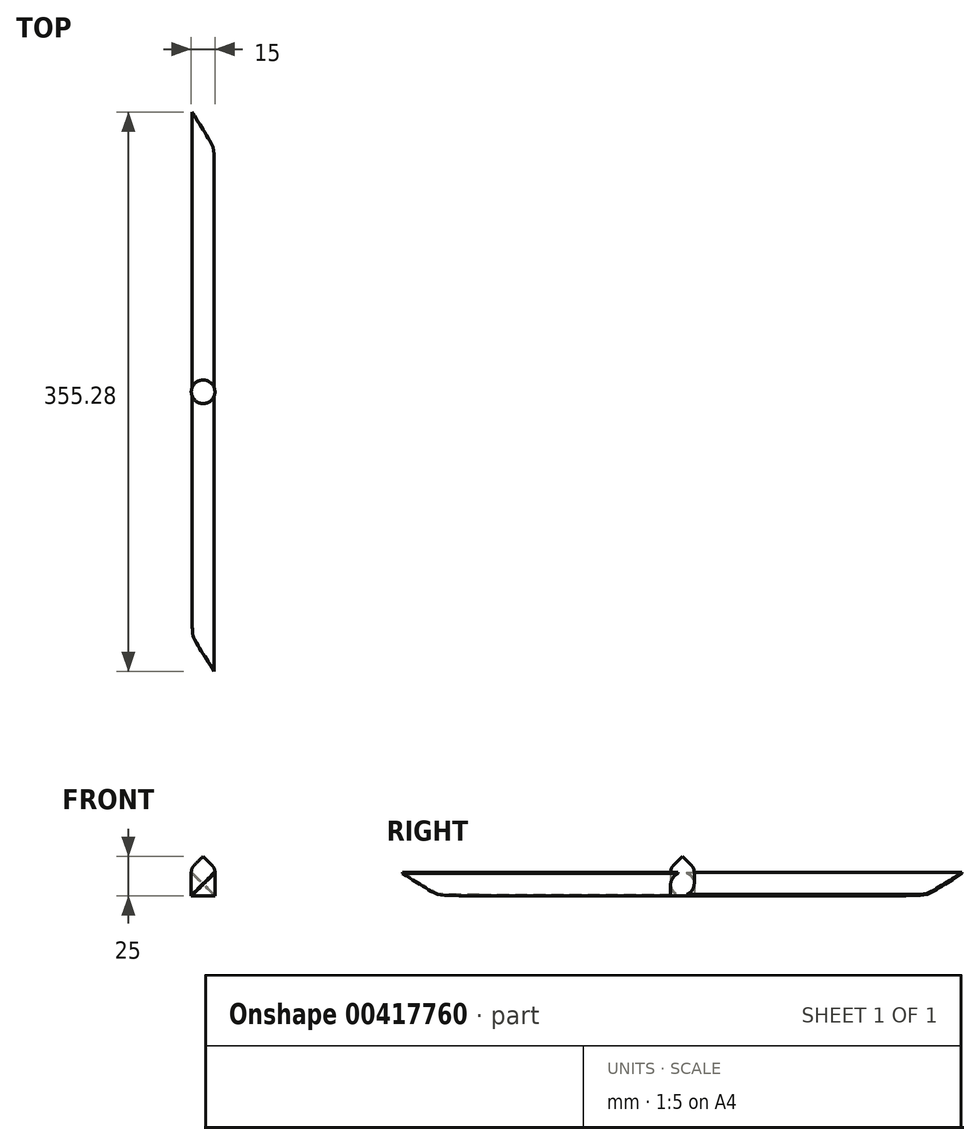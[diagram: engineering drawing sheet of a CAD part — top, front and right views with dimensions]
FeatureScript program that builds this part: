
annotation { "Feature Type Name" : "Feature", "Feature Type Description" : "" }
export const myFeature = defineFeature(function(context is Context, id is Id, definition is map)
    precondition{}
    {
        {
            var Q0;
            Q0=qCreatedBy(makeId("Top.planeOp"),FACE);
            var sketch = newSketch(context, id + "F0", { "sketchPlane" : qUnion([Q0])});
            skCircle(sketch, "E0", {"center": v(0, 0) * mm, "radius": 7.5 * mm});
            skLineSegment(sketch, "E1.bottom", {"start": v(7, -177.64) * mm, "end": v(-7, -177.64) * mm});
            skLineSegment(sketch, "E1.top", {"start": v(7, 177.64) * mm, "end": v(-7, 177.64) * mm});
            skLineSegment(sketch, "E1.left", {"start": v(7, -177.64) * mm, "end": v(7, 177.64) * mm});
            skLineSegment(sketch, "E1.right", {"start": v(-7, -177.64) * mm, "end": v(-7, 177.64) * mm});
            skPoint(sketch, "E2.positionSnap0", {"position": v(0, 177.64) * mm});
            skSolve(sketch);
        }
        {
            var Q0;
            {var subQ0=sQuery(id+"F0.wireOp",EDGE,"E0");var subQ1=makeQuery(id+"F0.imprint","INTERSECT",VERTEX,{"derivedFrom":[subQ0,sQuery(id+"F0.wireOp",EDGE,"E1.left")]});Q0=makeQuery(id+"F0.imprint","IMPRINT",FACE,{"disambiguationData":[TD([[makeQuery(id+"F0.imprint","IMPRINT",EDGE,{"disambiguationData":[TD([[subQ1,-1.0]])],"derivedFrom":subQ0}),1.0]])]});}
            var Q1;
            {var subQ0=sQuery(id+"F0.wireOp",EDGE,"E1.right");var subQ1=sQuery(id+"F0.wireOp",EDGE,"E0");var subQ2=makeQuery(id+"F0.imprint","INTERSECT",VERTEX,{"disambiguationData":[OD(0.0)],"derivedFrom":[subQ1,subQ0]});Q1=makeQuery(id+"F0.imprint","IMPRINT",FACE,{"disambiguationData":[TD([[makeQuery(id+"F0.imprint","IMPRINT",EDGE,{"disambiguationData":[TD([[subQ2,1.0]])],"derivedFrom":subQ1}),1.0]])]});}
            var Q2;
            {var subQ0=sQuery(id+"F0.wireOp",EDGE,"E1.right");var subQ1=sQuery(id+"F0.wireOp",EDGE,"E0");var subQ2=makeQuery(id+"F0.imprint","INTERSECT",VERTEX,{"disambiguationData":[OD(0.0)],"derivedFrom":[subQ1,subQ0]});Q2=makeQuery(id+"F0.imprint","IMPRINT",FACE,{"disambiguationData":[TD([[makeQuery(id+"F0.imprint","IMPRINT",EDGE,{"disambiguationData":[TD([[subQ2,-1.0]])],"derivedFrom":subQ1}),1.0]])]});}
            extrude(context, id + "F1", {"entities" : qUnion([Q0, Q1, Q2]), "depth" : 25 * mm});
        }
        {
            var Q0;
            Q0=makeQuery(id+"F1.opExtrude","CAP_EDGE",EDGE,{"disambiguationData":[OSD([sQuery(id+"F0.wireOp",EDGE,"E0")])],"isStart":false});
            chamfer(context, id + "F2", {"entities" : qUnion([Q0]), "width" : 7.5 * mm, "tangentPropagation" : true});
        }
        {
            var Q0;
            Q0 = qSketchRegion(id + "F0", true);
            extrude(context, id + "F3", {"entities" : qUnion([Q0]), "operationType" : NewBodyOperationType.ADD, "depth" : 15 * mm});
        }
        {
            var Q0;
            {var subQ0=sQuery(id+"F0.wireOp",EDGE,"E0");Q0=makeQuery(id+"F2.opChamfer","BLEND_EDGE",EDGE,{"blendedFrom":[makeQuery(id+"F1.opExtrude","CAP_EDGE",EDGE,{"disambiguationData":[OSD([subQ0])],"isStart":false}),makeQuery(id+"F1.opExtrude","SWEPT_FACE",FACE,{"disambiguationData":[OSD([subQ0])]})],"blendedInto":[makeQuery(id+"F1.opExtrude","SWEPT_FACE",FACE,{"disambiguationData":[OSD([subQ0])]})]});}
            fillet(context, id + "F4", {"entities" : qUnion([Q0]), "radius" : 6 * mm, "tangentPropagation" : true, "allowEdgeOverflow" : false});
        }
        {
            var Q0;
            {var subQ0=sQuery(id+"F0.wireOp",EDGE,"E1.right");Q0=makeQuery(id+"F3.opExtrude","CAP_EDGE",EDGE,{"disambiguationData":[OSD([subQ0]),TDD([makeQuery(id+"F0.imprint","IMPRINT",EDGE,{"disambiguationData":[TD([[makeQuery(id+"F0.imprint","INTERSECT",VERTEX,{"derivedFrom":[sQuery(id+"F0.wireOp",EDGE,"E1.bottom"),subQ0]}),-1.0]])],"derivedFrom":subQ0})])],"isStart":false});}
            var Q1;
            {var subQ0=sQuery(id+"F0.wireOp",EDGE,"E1.left");Q1=makeQuery(id+"F3.opExtrude","CAP_EDGE",EDGE,{"disambiguationData":[OSD([subQ0]),TDD([makeQuery(id+"F0.imprint","IMPRINT",EDGE,{"disambiguationData":[TD([[makeQuery(id+"F0.imprint","INTERSECT",VERTEX,{"derivedFrom":[sQuery(id+"F0.wireOp",EDGE,"E1.bottom"),subQ0]}),-1.0]])],"derivedFrom":subQ0})])],"isStart":true});}
            var Q2;
            {var subQ0=sQuery(id+"F0.wireOp",EDGE,"E1.left");Q2=makeQuery(id+"F3.opExtrude","CAP_EDGE",EDGE,{"disambiguationData":[OSD([subQ0]),TDD([makeQuery(id+"F0.imprint","IMPRINT",EDGE,{"disambiguationData":[TD([[makeQuery(id+"F0.imprint","INTERSECT",VERTEX,{"derivedFrom":[sQuery(id+"F0.wireOp",EDGE,"E1.top"),subQ0]}),1.0]])],"derivedFrom":subQ0})])],"isStart":false});}
            var Q3;
            {var subQ0=sQuery(id+"F0.wireOp",EDGE,"E1.right");Q3=makeQuery(id+"F3.opExtrude","CAP_EDGE",EDGE,{"disambiguationData":[OSD([subQ0]),TDD([makeQuery(id+"F0.imprint","IMPRINT",EDGE,{"disambiguationData":[TD([[makeQuery(id+"F0.imprint","INTERSECT",VERTEX,{"derivedFrom":[sQuery(id+"F0.wireOp",EDGE,"E1.top"),subQ0]}),1.0]])],"derivedFrom":subQ0})])],"isStart":true});}
            chamfer(context, id + "F5", {"entities" : qUnion([Q0, Q1, Q2, Q3]), "width" : 14.1 * mm, "tangentPropagation" : true});
        }
        {
            var Q0;
            Q0=makeQuery(id+"F3.opExtrude","SWEPT_EDGE",EDGE,{"disambiguationData":[OSD([sQuery(id+"F0.wireOp",EDGE,"E1.bottom"),sQuery(id+"F0.wireOp",EDGE,"E1.right")])]});
            var Q1;
            Q1=makeQuery(id+"F3.opExtrude","SWEPT_EDGE",EDGE,{"disambiguationData":[OSD([sQuery(id+"F0.wireOp",EDGE,"E1.top"),sQuery(id+"F0.wireOp",EDGE,"E1.left")])]});
            fillet(context, id + "F6", {"entities" : qUnion([Q0, Q1]), "radius" : 91.02 * mm, "tangentPropagation" : true, "rho" : 0.9, "crossSection" : FilletCrossSection.CONIC, "allowEdgeOverflow" : false});
        }
    });
